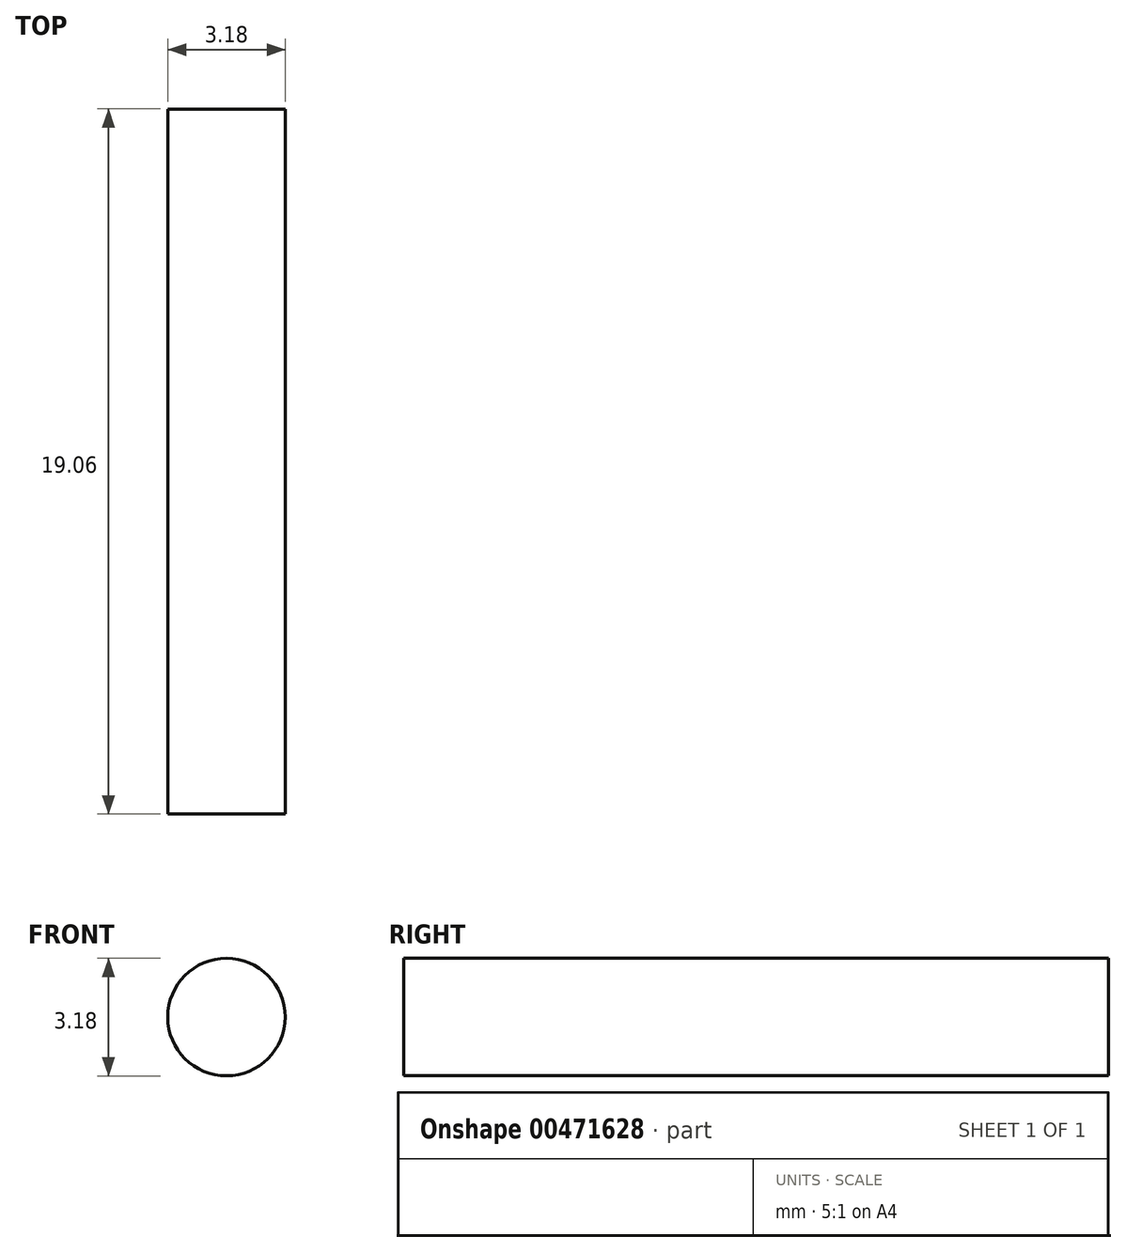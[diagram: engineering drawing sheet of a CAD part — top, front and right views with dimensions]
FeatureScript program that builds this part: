
annotation { "Feature Type Name" : "Feature", "Feature Type Description" : "" }
export const myFeature = defineFeature(function(context is Context, id is Id, definition is map)
    precondition{}
    {
        {
            var Q0;
            Q0=qCreatedBy(makeId("Front.planeOp"),FACE);
            var sketch = newSketch(context, id + "F0", { "sketchPlane" : qUnion([Q0])});
            skCircle(sketch, "E0", {"center": v(0, 0) * mm, "radius": 1.59 * mm});
            skSolve(sketch);
        }
        {
            var Q0;
            Q0 = qSketchRegion(id + "F0", true);
            extrude(context, id + "F1", {"entities" : qUnion([Q0]), "depth" : 19.05 * mm, "symmetric" : true});
        }
    });
